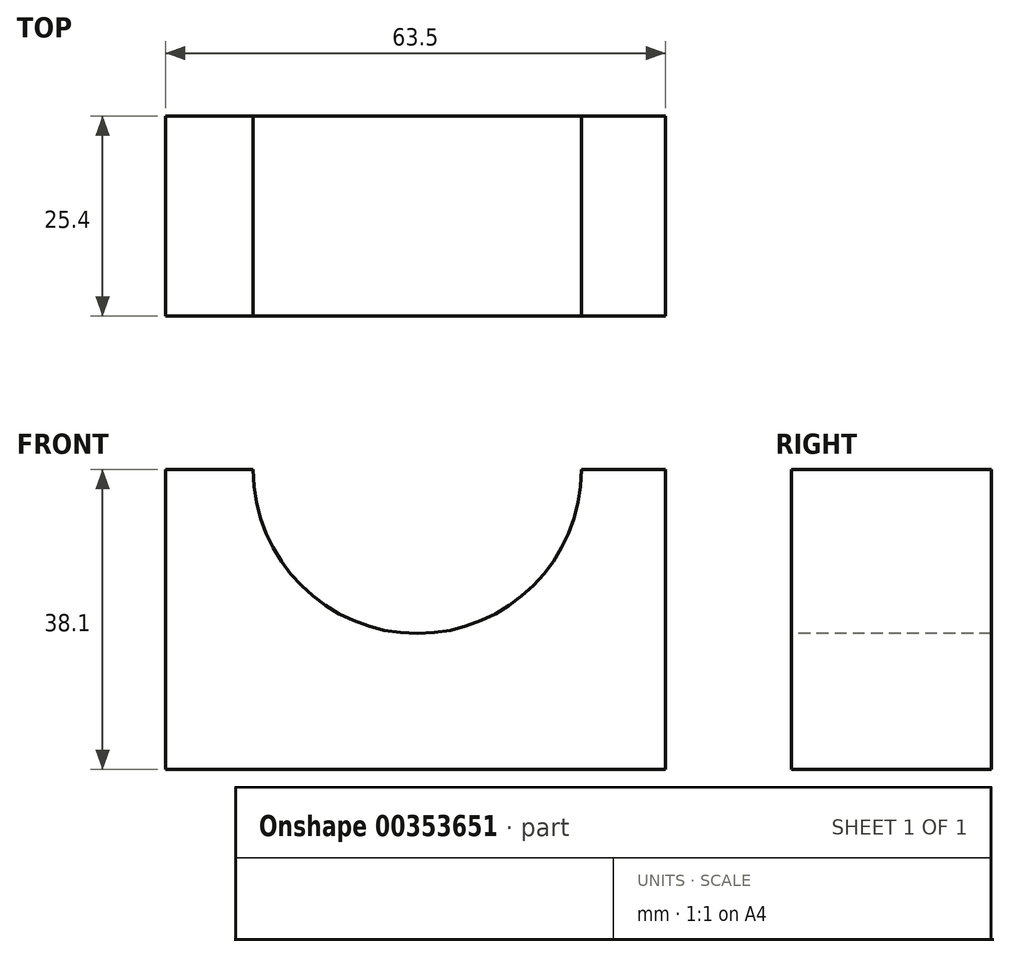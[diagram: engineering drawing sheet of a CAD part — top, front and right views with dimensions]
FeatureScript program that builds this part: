
annotation { "Feature Type Name" : "Feature", "Feature Type Description" : "" }
export const myFeature = defineFeature(function(context is Context, id is Id, definition is map)
    precondition{}
    {
        {
            var Q0;
            Q0=qCreatedBy(makeId("Front.planeOp"),FACE);
            var sketch = newSketch(context, id + "F0", { "sketchPlane" : qUnion([Q0])});
            skLineSegment(sketch, "E0", {"start": v(-85.44, 0) * mm, "end": v(-85.44, 38.1) * mm});
            skLineSegment(sketch, "E1", {"start": v(-85.44, 38.1) * mm, "end": v(-21.94, 38.1) * mm});
            skLineSegment(sketch, "E2", {"start": v(-21.94, 38.1) * mm, "end": v(-21.94, 0) * mm});
            skLineSegment(sketch, "E3", {"start": v(-85.44, 0) * mm, "end": v(-21.94, 0) * mm});
            skSolve(sketch);
        }
        {
            var Q0;
            Q0=makeQuery(id+"F0.imprint","IMPRINT",FACE,{"disambiguationData":[TD([[makeQuery(id+"F0.imprint","IMPRINT",EDGE,{"derivedFrom":sQuery(id+"F0.wireOp",EDGE,"E0")}),-1.0]])]});
            extrude(context, id + "F1", {"entities" : qUnion([Q0]), "depth" : 25.4 * mm});
        }
        {
            var Q0;
            Q0=makeQuery(id+"F1.opExtrude","CAP_FACE",FACE,{"disambiguationData":[OSD([sQuery(id+"F0.wireOp",EDGE,"E0"),sQuery(id+"F0.wireOp",EDGE,"E1"),sQuery(id+"F0.wireOp",EDGE,"E2"),sQuery(id+"F0.wireOp",EDGE,"E3")])],"isStart":false});
            var sketch = newSketch(context, id + "F2", { "sketchPlane" : qUnion([Q0])});
            skArc(sketch, "E4", {"start": v(-74.3, 38.1) * mm, "mid": v(-53.46, 17.27) * mm, "end": v(-32.63, 38.1) * mm});
            skSolve(sketch);
        }
        {
            var Q0;
            Q0 = qSketchRegion(id + "F2", true);
            var Q1;
            {var subQ0=sQuery(id+"F2.wireOp",EDGE,"E4");Q1=makeQuery(id+"F2.imprint","IMPRINT",FACE,{"disambiguationData":[TD([[makeQuery(id+"F2.imprint","IMPRINT",EDGE,{"derivedFrom":subQ0}),1.0]])]});}
            extrude(context, id + "F3", {"entities" : qUnion([Q0, Q1]), "operationType" : NewBodyOperationType.REMOVE, "oppositeDirection" : true, "depth" : 25.4 * mm});
        }
    });
